annotation { "Feature Type Name" : "Feature", "Feature Type Description" : "" }
export const myFeature = defineFeature(function(context is Context, id is Id, definition is map)
    precondition{}
    {
        {
            var Q0;
            Q0=qCreatedBy(makeId("Top.planeOp"),FACE);
            var sketch = newSketch(context, id + "F0", { "sketchPlane" : qUnion([Q0])});
            skLineSegment(sketch, "E0.bottom", {"start": v(0, 0) * mm, "end": v(112.25, 0) * mm});
            skLineSegment(sketch, "E0.top", {"start": v(0, 107.75) * mm, "end": v(112.25, 107.75) * mm});
            skLineSegment(sketch, "E0.left", {"start": v(0, 0) * mm, "end": v(0, 107.75) * mm});
            skLineSegment(sketch, "E0.right", {"start": v(112.25, 0) * mm, "end": v(112.25, 107.75) * mm});
            skCircle(sketch, "E1", {"center": v(3.5, 3.5) * mm, "radius": 2.25 * mm});
            skCircle(sketch, "E2", {"center": v(108.75, 3.5) * mm, "radius": 2.25 * mm});
            skCircle(sketch, "E3", {"center": v(92.23, 18.3) * mm, "radius": 10.5 * mm});
            skCircle(sketch, "E4", {"center": v(60, 18.3) * mm, "radius": 3 * mm});
            skLineSegment(sketch, "E5.bottom", {"start": v(68.73, 26.3) * mm, "end": v(78.73, 26.3) * mm});
            skLineSegment(sketch, "E5.top", {"start": v(68.73, 24.3) * mm, "end": v(78.73, 24.3) * mm});
            skLineSegment(sketch, "E5.left", {"start": v(68.73, 26.3) * mm, "end": v(68.73, 24.3) * mm});
            skLineSegment(sketch, "E5.right", {"start": v(78.73, 26.3) * mm, "end": v(78.73, 24.3) * mm});
            skLineSegment(sketch, "E6.1.0.0", {"start": v(78.8, 22.4) * mm, "end": v(78.8, 20.4) * mm});
            skLineSegment(sketch, "E6.1.0.1", {"start": v(68.8, 22.4) * mm, "end": v(68.8, 20.4) * mm});
            skLineSegment(sketch, "E6.1.0.2", {"start": v(68.8, 22.4) * mm, "end": v(78.8, 22.4) * mm});
            skLineSegment(sketch, "E6.1.0.3", {"start": v(68.8, 20.4) * mm, "end": v(78.8, 20.4) * mm});
            skLineSegment(sketch, "E6.2.0.0", {"start": v(78.87, 18.5) * mm, "end": v(78.87, 16.5) * mm});
            skLineSegment(sketch, "E6.2.0.1", {"start": v(68.87, 18.5) * mm, "end": v(68.87, 16.5) * mm});
            skLineSegment(sketch, "E6.2.0.2", {"start": v(68.87, 18.5) * mm, "end": v(78.87, 18.5) * mm});
            skLineSegment(sketch, "E6.2.0.3", {"start": v(68.87, 16.5) * mm, "end": v(78.87, 16.5) * mm});
            skLineSegment(sketch, "E6.3.0.0", {"start": v(78.93, 14.62) * mm, "end": v(78.93, 12.62) * mm});
            skLineSegment(sketch, "E6.3.0.1", {"start": v(68.93, 14.62) * mm, "end": v(68.93, 12.62) * mm});
            skLineSegment(sketch, "E6.3.0.2", {"start": v(68.93, 14.62) * mm, "end": v(78.93, 14.62) * mm});
            skLineSegment(sketch, "E6.3.0.3", {"start": v(68.93, 12.62) * mm, "end": v(78.93, 12.62) * mm});
            skLineSegment(sketch, "E6.4.0.0", {"start": v(79, 10.73) * mm, "end": v(79, 8.73) * mm});
            skLineSegment(sketch, "E6.4.0.1", {"start": v(69, 10.73) * mm, "end": v(69, 8.73) * mm});
            skLineSegment(sketch, "E6.4.0.2", {"start": v(69, 10.73) * mm, "end": v(79, 10.73) * mm});
            skLineSegment(sketch, "E6.4.0.3", {"start": v(69, 8.73) * mm, "end": v(79, 8.73) * mm});
            skLineSegment(sketch, "E6.direction1", {"start": v(68.73, 24.3) * mm, "end": v(68.8, 20.4) * mm, "construction": true});
            skSolve(sketch);
        }
        {
            var Q0;
            Q0=qSketchRegion(id+"F0",true);
            extrude(context, id + "F1", {"entities" : qUnion([Q0]), "depth" : 2 * mm, "offsetDistance" : 25 * mm});
        }
        {
            var Q0;
            Q0=makeQuery(id+"F1.opExtrude","CAP_FACE",FACE,{"disambiguationData":[OSD([sQuery(id+"F0.wireOp",EDGE,"E0.bottom"),sQuery(id+"F0.wireOp",EDGE,"E0.top"),sQuery(id+"F0.wireOp",EDGE,"E0.left"),sQuery(id+"F0.wireOp",EDGE,"E0.right"),sQuery(id+"F0.wireOp",EDGE,"VJWhoFmN-CNNd-a6gC-JCuR-XAWFigalHExP"),sQuery(id+"F0.wireOp",EDGE,"vIjKD9R8-VXcQ-Syzh-FnhK-4sEpH6Cil4JO"),sQuery(id+"F0.wireOp",EDGE,"E1"),sQuery(id+"F0.wireOp",EDGE,"E2"),sQuery(id+"F0.wireOp",EDGE,"RQaqiYP4-0Fcv-lfBv-gB3g-qDtZXz7Vt3Ng.bottom"),sQuery(id+"F0.wireOp",EDGE,"RQaqiYP4-0Fcv-lfBv-gB3g-qDtZXz7Vt3Ng.top"),sQuery(id+"F0.wireOp",EDGE,"RQaqiYP4-0Fcv-lfBv-gB3g-qDtZXz7Vt3Ng.left"),sQuery(id+"F0.wireOp",EDGE,"RQaqiYP4-0Fcv-lfBv-gB3g-qDtZXz7Vt3Ng.right"),sQuery(id+"F0.wireOp",EDGE,"E3"),sQuery(id+"F0.wireOp",EDGE,"E4"),sQuery(id+"F0.wireOp",EDGE,"A4T1cfBq-erl5-skMh-XZ60-SgpOEBQzwWt8"),sQuery(id+"F0.wireOp",EDGE,"E5.bottom"),sQuery(id+"F0.wireOp",EDGE,"E5.top"),sQuery(id+"F0.wireOp",EDGE,"E5.left"),sQuery(id+"F0.wireOp",EDGE,"E5.right"),sQuery(id+"F0.wireOp",EDGE,"E6.1.0.0"),sQuery(id+"F0.wireOp",EDGE,"E6.1.0.1"),sQuery(id+"F0.wireOp",EDGE,"E6.1.0.2"),sQuery(id+"F0.wireOp",EDGE,"E6.1.0.3"),sQuery(id+"F0.wireOp",EDGE,"E6.2.0.0"),sQuery(id+"F0.wireOp",EDGE,"E6.2.0.1"),sQuery(id+"F0.wireOp",EDGE,"E6.2.0.2"),sQuery(id+"F0.wireOp",EDGE,"E6.2.0.3"),sQuery(id+"F0.wireOp",EDGE,"E6.3.0.0"),sQuery(id+"F0.wireOp",EDGE,"E6.3.0.1"),sQuery(id+"F0.wireOp",EDGE,"E6.3.0.2"),sQuery(id+"F0.wireOp",EDGE,"E6.3.0.3"),sQuery(id+"F0.wireOp",EDGE,"E6.4.0.0"),sQuery(id+"F0.wireOp",EDGE,"E6.4.0.1"),sQuery(id+"F0.wireOp",EDGE,"E6.4.0.2"),sQuery(id+"F0.wireOp",EDGE,"E6.4.0.3")])],"isStart":false});
            var sketch = newSketch(context, id + "F2", { "sketchPlane" : qUnion([Q0])});
            skLineSegment(sketch, "E7.bottom", {"start": v(49.13, 110.75) * mm, "end": v(61.13, 110.75) * mm});
            skLineSegment(sketch, "E7.top", {"start": v(49.13, 104.75) * mm, "end": v(61.13, 104.75) * mm});
            skLineSegment(sketch, "E7.left", {"start": v(49.13, 110.75) * mm, "end": v(49.13, 104.75) * mm});
            skLineSegment(sketch, "E7.right", {"start": v(61.13, 110.75) * mm, "end": v(61.13, 104.75) * mm});
            skSolve(sketch);
        }
        {
            var Q0;
            Q0=qSketchRegion(id+"F2",true);
            extrude(context, id + "F3", {"entities" : qUnion([Q0]), "operationType" : NewBodyOperationType.REMOVE, "endBound" : BoundingType.THROUGH_ALL, "oppositeDirection" : true, "depth" : 3 * mm, "offsetDistance" : 25 * mm});
        }
        {
            var Q0;
            {var subQ27=sQuery(id+"F0.wireOp",EDGE,"E0.left");var subQ29=sQuery(id+"F0.wireOp",EDGE,"E0.bottom");Q0=makeQuery(id+"F3.boolean.opBoolean","SPLIT",FACE,{"disambiguationData":[TD([makeQuery(id+"F1.opExtrude","SWEPT_FACE",FACE,{"disambiguationData":[OSD([subQ27])]})])],"derivedFrom":makeQuery(id+"F1.opExtrude","SWEPT_FACE",FACE,{"disambiguationData":[OSD([subQ29])]})});}
            var Q1;
            {var subQ26=sQuery(id+"F0.wireOp",EDGE,"E0.right");var subQ29=sQuery(id+"F0.wireOp",EDGE,"E0.bottom");Q1=makeQuery(id+"F3.boolean.opBoolean","SPLIT",FACE,{"disambiguationData":[TD([makeQuery(id+"F1.opExtrude","SWEPT_FACE",FACE,{"disambiguationData":[OSD([subQ26])]})])],"derivedFrom":makeQuery(id+"F1.opExtrude","SWEPT_FACE",FACE,{"disambiguationData":[OSD([subQ29])]})});}
            extrude(context, id + "F4", {"entities" : qUnion([Q0, Q1]), "operationType" : NewBodyOperationType.ADD, "depth" : 6 * mm, "offsetDistance" : 25 * mm});
        }
        {
            var Q0;
            {var subQ27=sQuery(id+"F0.wireOp",EDGE,"E0.left");var subQ28=sQuery(id+"F0.wireOp",EDGE,"E0.top");Q0=makeQuery(id+"F3.boolean.opBoolean","SPLIT",FACE,{"disambiguationData":[TD([makeQuery(id+"F1.opExtrude","SWEPT_FACE",FACE,{"disambiguationData":[OSD([subQ28])]})])],"derivedFrom":makeQuery(id+"F1.opExtrude","SWEPT_FACE",FACE,{"disambiguationData":[OSD([subQ27])]})});}
            var Q1;
            {var subQ0=sQuery(id+"F0.wireOp",EDGE,"E0.left");var subQ1=sQuery(id+"F0.wireOp",EDGE,"E0.bottom");Q1=makeQuery(id+"F4.boolean.opBoolean","MERGE",FACE,{"derivedFrom":[makeQuery(id+"F3.boolean.opBoolean","SPLIT",FACE,{"disambiguationData":[TD([makeQuery(id+"F1.opExtrude","SWEPT_FACE",FACE,{"disambiguationData":[OSD([subQ1])]})])],"derivedFrom":makeQuery(id+"F1.opExtrude","SWEPT_FACE",FACE,{"disambiguationData":[OSD([subQ0])]})}),makeQuery(id+"F4.opExtrude","SWEPT_FACE",FACE,{"disambiguationData":[OSD([subQ1,subQ0])]})]});}
            extrude(context, id + "F5", {"entities" : qUnion([Q0, Q1]), "operationType" : NewBodyOperationType.ADD, "depth" : 6 * mm, "offsetDistance" : 25 * mm});
        }
        {
            var Q0;
            {var subQ26=sQuery(id+"F0.wireOp",EDGE,"E0.right");var subQ28=sQuery(id+"F0.wireOp",EDGE,"E0.top");Q0=makeQuery(id+"F3.boolean.opBoolean","SPLIT",FACE,{"disambiguationData":[TD([makeQuery(id+"F1.opExtrude","SWEPT_FACE",FACE,{"disambiguationData":[OSD([subQ28])]})])],"derivedFrom":makeQuery(id+"F1.opExtrude","SWEPT_FACE",FACE,{"disambiguationData":[OSD([subQ26])]})});}
            var Q1;
            {var subQ0=sQuery(id+"F0.wireOp",EDGE,"E0.right");var subQ1=sQuery(id+"F0.wireOp",EDGE,"E0.bottom");Q1=makeQuery(id+"F4.boolean.opBoolean","MERGE",FACE,{"derivedFrom":[makeQuery(id+"F3.boolean.opBoolean","SPLIT",FACE,{"disambiguationData":[TD([makeQuery(id+"F1.opExtrude","SWEPT_FACE",FACE,{"disambiguationData":[OSD([subQ1])]})])],"derivedFrom":makeQuery(id+"F1.opExtrude","SWEPT_FACE",FACE,{"disambiguationData":[OSD([subQ0])]})}),makeQuery(id+"F4.opExtrude","SWEPT_FACE",FACE,{"disambiguationData":[OSD([subQ1,subQ0])]})]});}
            extrude(context, id + "F6", {"entities" : qUnion([Q0, Q1]), "operationType" : NewBodyOperationType.ADD, "depth" : 6 * mm, "offsetDistance" : 25 * mm});
        }
        {
            var Q0;
            {var subQ0=sQuery(id+"F0.wireOp",EDGE,"E0.right");var subQ1=sQuery(id+"F0.wireOp",EDGE,"E0.bottom");var subQ2=makeQuery(id+"F1.opExtrude","SWEPT_FACE",FACE,{"disambiguationData":[OSD([subQ1])]});var subQ3=makeQuery(id+"F1.opExtrude","SWEPT_FACE",FACE,{"disambiguationData":[OSD([subQ0])]});var subQ4=sQuery(id+"F0.wireOp",EDGE,"E0.left");var subQ5=sQuery(id+"F0.wireOp",EDGE,"E0.top");var subQ6=makeQuery(id+"F1.opExtrude","CAP_FACE",FACE,{"disambiguationData":[OSD([subQ1,subQ5,subQ4,subQ0,sQuery(id+"F0.wireOp",EDGE,"VJWhoFmN-CNNd-a6gC-JCuR-XAWFigalHExP"),sQuery(id+"F0.wireOp",EDGE,"vIjKD9R8-VXcQ-Syzh-FnhK-4sEpH6Cil4JO"),sQuery(id+"F0.wireOp",EDGE,"E1"),sQuery(id+"F0.wireOp",EDGE,"E2"),sQuery(id+"F0.wireOp",EDGE,"E3"),sQuery(id+"F0.wireOp",EDGE,"E4"),sQuery(id+"F0.wireOp",EDGE,"E5.bottom"),sQuery(id+"F0.wireOp",EDGE,"E5.top"),sQuery(id+"F0.wireOp",EDGE,"E5.left"),sQuery(id+"F0.wireOp",EDGE,"E5.right"),sQuery(id+"F0.wireOp",EDGE,"E6.1.0.0"),sQuery(id+"F0.wireOp",EDGE,"E6.1.0.1"),sQuery(id+"F0.wireOp",EDGE,"E6.1.0.2"),sQuery(id+"F0.wireOp",EDGE,"E6.1.0.3"),sQuery(id+"F0.wireOp",EDGE,"E6.2.0.0"),sQuery(id+"F0.wireOp",EDGE,"E6.2.0.1"),sQuery(id+"F0.wireOp",EDGE,"E6.2.0.2"),sQuery(id+"F0.wireOp",EDGE,"E6.2.0.3"),sQuery(id+"F0.wireOp",EDGE,"E6.3.0.0"),sQuery(id+"F0.wireOp",EDGE,"E6.3.0.1"),sQuery(id+"F0.wireOp",EDGE,"E6.3.0.2"),sQuery(id+"F0.wireOp",EDGE,"E6.3.0.3"),sQuery(id+"F0.wireOp",EDGE,"E6.4.0.0"),sQuery(id+"F0.wireOp",EDGE,"E6.4.0.1"),sQuery(id+"F0.wireOp",EDGE,"E6.4.0.2"),sQuery(id+"F0.wireOp",EDGE,"E6.4.0.3")])],"isStart":true});var subQ7=makeQuery(id+"F1.opExtrude","CAP_EDGE",EDGE,{"disambiguationData":[OSD([subQ0])],"isStart":true});var subQ8=makeQuery(id+"F1.opExtrude","SWEPT_FACE",FACE,{"disambiguationData":[OSD([subQ5])]});var subQ9=makeQuery(id+"F1.opExtrude","SWEPT_FACE",FACE,{"disambiguationData":[OSD([subQ4])]});var subQ10=makeQuery(id+"F1.opExtrude","CAP_EDGE",EDGE,{"disambiguationData":[OSD([subQ4])],"isStart":true});var subQ11=makeQuery(id+"F1.opExtrude","CAP_EDGE",EDGE,{"disambiguationData":[OSD([subQ1])],"isStart":true});Q0=makeQuery(id+"F6.boolean.opBoolean","MERGE",FACE,{"derivedFrom":[makeQuery(id+"F5.boolean.opBoolean","MERGE",FACE,{"derivedFrom":[makeQuery(id+"F4.boolean.opBoolean","MERGE",FACE,{"derivedFrom":[subQ6,makeQuery(id+"F4.opExtrude","SWEPT_FACE",FACE,{"disambiguationData":[OSD([subQ1]),TDD([makeQuery(id+"F3.boolean.opBoolean","SPLIT",EDGE,{"disambiguationData":[TD([subQ9])],"derivedFrom":subQ11})])]}),makeQuery(id+"F4.opExtrude","SWEPT_FACE",FACE,{"disambiguationData":[OSD([subQ1]),TDD([makeQuery(id+"F3.boolean.opBoolean","SPLIT",EDGE,{"disambiguationData":[TD([subQ3])],"derivedFrom":subQ11})])]})]}),makeQuery(id+"F5.opExtrude","SWEPT_FACE",FACE,{"disambiguationData":[OSD([subQ4]),TDD([makeQuery(id+"F3.boolean.opBoolean","SPLIT",EDGE,{"disambiguationData":[TD([subQ8])],"derivedFrom":subQ10})])]}),makeQuery(id+"F5.opExtrude","SWEPT_FACE",FACE,{"disambiguationData":[OSD([subQ1,subQ4]),TDD([makeQuery(id+"F4.boolean.opBoolean","MERGE",EDGE,{"derivedFrom":[makeQuery(id+"F3.boolean.opBoolean","SPLIT",EDGE,{"disambiguationData":[TD([subQ2])],"derivedFrom":subQ10}),makeQuery(id+"F4.opExtrude","SWEPT_EDGE",EDGE,{"disambiguationData":[OSD([subQ1,subQ4]),TDD([makeQuery(id+"F1.opExtrude","CAP_VERTEX",VERTEX,{"disambiguationData":[OSD([subQ1,subQ4])],"isStart":true})])]})]})])]})]}),makeQuery(id+"F6.opExtrude","SWEPT_FACE",FACE,{"disambiguationData":[OSD([subQ0]),TDD([makeQuery(id+"F3.boolean.opBoolean","SPLIT",EDGE,{"disambiguationData":[TD([subQ8])],"derivedFrom":subQ7})])]}),makeQuery(id+"F6.opExtrude","SWEPT_FACE",FACE,{"disambiguationData":[OSD([subQ1,subQ0]),TDD([makeQuery(id+"F4.boolean.opBoolean","MERGE",EDGE,{"derivedFrom":[makeQuery(id+"F3.boolean.opBoolean","SPLIT",EDGE,{"disambiguationData":[TD([subQ2])],"derivedFrom":subQ7}),makeQuery(id+"F4.opExtrude","SWEPT_EDGE",EDGE,{"disambiguationData":[OSD([subQ1,subQ0]),TDD([makeQuery(id+"F1.opExtrude","CAP_VERTEX",VERTEX,{"disambiguationData":[OSD([subQ1,subQ0])],"isStart":true})])]})]})])]})]});}
            var sketch = newSketch(context, id + "F7", { "sketchPlane" : qUnion([Q0])});
            skLineSegment(sketch, "E8.bottom", {"start": v(118.25, -107.75) * mm, "end": v(116.75, -107.75) * mm});
            skLineSegment(sketch, "E8.top", {"start": v(118.25, 6) * mm, "end": v(116.75, 6) * mm});
            skLineSegment(sketch, "E8.left", {"start": v(118.25, -107.75) * mm, "end": v(118.25, -107.75) * mm});
            skLineSegment(sketch, "E8.right", {"start": v(116.75, -107.75) * mm, "end": v(116.75, -58.87) * mm});
            skLineSegment(sketch, "E9.bottom", {"start": v(-6, -107.75) * mm, "end": v(-4.5, -107.75) * mm});
            skLineSegment(sketch, "E9.top", {"start": v(-6, 6) * mm, "end": v(-4.5, 6) * mm});
            skLineSegment(sketch, "E9.left", {"start": v(-6, -107.75) * mm, "end": v(-6, -107.75) * mm});
            skLineSegment(sketch, "E9.right", {"start": v(-4.5, -107.75) * mm, "end": v(-4.5, -58.87) * mm});
            skLineSegment(sketch, "E10.bottom", {"start": v(116.75, 4.5) * mm, "end": v(61.13, 4.5) * mm});
            skLineSegment(sketch, "E10.top", {"start": v(116.75, 6) * mm, "end": v(61.13, 6) * mm});
            skLineSegment(sketch, "E11.trimOffspring", {"start": v(61.13, 4.5) * mm, "end": v(-4.5, 4.5) * mm});
            skLineSegment(sketch, "E12.trimOffspring", {"start": v(61.13, 6) * mm, "end": v(-4.5, 6) * mm});
            skLineSegment(sketch, "E13.trimOffspring", {"start": v(118.25, -107.75) * mm, "end": v(118.25, 6) * mm});
            skLineSegment(sketch, "E14.trimOffspring", {"start": v(116.75, -58.87) * mm, "end": v(116.75, 4.5) * mm});
            skLineSegment(sketch, "E15.trimOffspring", {"start": v(-4.5, -58.87) * mm, "end": v(-4.5, 4.5) * mm});
            skLineSegment(sketch, "E16.trimOffspring", {"start": v(-6, -107.75) * mm, "end": v(-6, 6) * mm});
            skSolve(sketch);
        }
        {
            var Q0;
            {var subQ43=sQuery(id+"F7.wireOp",EDGE,"E9.top");Q0=makeQuery(id+"F7.imprint","IMPRINT",FACE,{"disambiguationData":[TD([[makeQuery(id+"F7.imprint","IMPRINT",EDGE,{"derivedFrom":subQ43}),-1.0]])]});}
            var Q1;
            {var subQ0=sQuery(id+"F7.wireOp",EDGE,"E11.trimOffspring");var subQ2=sQuery(id+"F0.wireOp",EDGE,"E6.4.0.3");var subQ3=sQuery(id+"F0.wireOp",EDGE,"E6.4.0.2");var subQ4=sQuery(id+"F0.wireOp",EDGE,"E6.4.0.1");var subQ5=sQuery(id+"F0.wireOp",EDGE,"E6.4.0.0");var subQ6=sQuery(id+"F0.wireOp",EDGE,"E6.3.0.3");var subQ7=sQuery(id+"F0.wireOp",EDGE,"E6.3.0.2");var subQ8=sQuery(id+"F0.wireOp",EDGE,"E6.3.0.1");var subQ9=sQuery(id+"F0.wireOp",EDGE,"E6.3.0.0");var subQ10=sQuery(id+"F0.wireOp",EDGE,"E6.2.0.3");var subQ11=sQuery(id+"F0.wireOp",EDGE,"E6.2.0.2");var subQ12=sQuery(id+"F0.wireOp",EDGE,"E6.2.0.1");var subQ13=sQuery(id+"F0.wireOp",EDGE,"E6.2.0.0");var subQ14=sQuery(id+"F0.wireOp",EDGE,"E6.1.0.3");var subQ15=sQuery(id+"F0.wireOp",EDGE,"E6.1.0.2");var subQ16=sQuery(id+"F0.wireOp",EDGE,"E6.1.0.1");var subQ17=sQuery(id+"F0.wireOp",EDGE,"E6.1.0.0");var subQ18=sQuery(id+"F0.wireOp",EDGE,"E5.right");var subQ19=sQuery(id+"F0.wireOp",EDGE,"E5.left");var subQ20=sQuery(id+"F0.wireOp",EDGE,"E5.top");var subQ21=sQuery(id+"F0.wireOp",EDGE,"E5.bottom");var subQ22=sQuery(id+"F0.wireOp",EDGE,"E4");var subQ23=sQuery(id+"F0.wireOp",EDGE,"E3");var subQ24=sQuery(id+"F0.wireOp",EDGE,"E2");var subQ25=sQuery(id+"F0.wireOp",EDGE,"E1");var subQ26=sQuery(id+"F0.wireOp",EDGE,"vIjKD9R8-VXcQ-Syzh-FnhK-4sEpH6Cil4JO");var subQ27=sQuery(id+"F0.wireOp",EDGE,"VJWhoFmN-CNNd-a6gC-JCuR-XAWFigalHExP");var subQ28=sQuery(id+"F0.wireOp",EDGE,"E0.right");var subQ29=sQuery(id+"F0.wireOp",EDGE,"E0.left");var subQ30=sQuery(id+"F0.wireOp",EDGE,"E0.top");var subQ31=sQuery(id+"F0.wireOp",EDGE,"E0.bottom");var subQ32=makeQuery(id+"F1.opExtrude","CAP_FACE",FACE,{"disambiguationData":[OSD([subQ31,subQ30,subQ29,subQ28,subQ27,subQ26,subQ25,subQ24,subQ23,subQ22,subQ21,subQ20,subQ19,subQ18,subQ17,subQ16,subQ15,subQ14,subQ13,subQ12,subQ11,subQ10,subQ9,subQ8,subQ7,subQ6,subQ5,subQ4,subQ3,subQ2])],"isStart":true});var subQ35=sQuery(id+"F2.wireOp",EDGE,"RaCBA7yH-dog8-7tBN-7lt1-G5SoJbxULKHr.left");var subQ36=makeQuery(id+"F4.boolean.opBoolean","MERGE",EDGE,{"derivedFrom":[makeQuery(id+"F3.boolean.opBoolean","INTERSECT",EDGE,{"derivedFrom":[subQ32,makeQuery(id+"F3.opExtrude","SWEPT_FACE",FACE,{"disambiguationData":[OSD([subQ35])]})]}),makeQuery(id+"F4.opExtrude","SWEPT_EDGE",EDGE,{"disambiguationData":[OSD([subQ31,subQ30,subQ29,subQ28,subQ27,subQ26,subQ25,subQ24,subQ23,subQ22,subQ21,subQ20,subQ19,subQ18,subQ17,subQ16,subQ15,subQ14,subQ13,subQ12,subQ11,subQ10,subQ9,subQ8,subQ7,subQ6,subQ5,subQ4,subQ3,subQ2,subQ35])]})]});var subQ37=makeQuery(id+"F7.imprint","INTERSECT",VERTEX,{"derivedFrom":[subQ36,subQ0]});Q1=makeQuery(id+"F7.imprint","IMPRINT",FACE,{"disambiguationData":[TD([[makeQuery(id+"F7.imprint","IMPRINT",EDGE,{"disambiguationData":[TD([[subQ37,1.0]])],"derivedFrom":subQ0}),-1.0]])]});}
            var Q2;
            {var subQ35=sQuery(id+"F7.wireOp",EDGE,"E8.top");Q2=makeQuery(id+"F7.imprint","IMPRINT",FACE,{"disambiguationData":[TD([[makeQuery(id+"F7.imprint","IMPRINT",EDGE,{"derivedFrom":subQ35}),-1.0]])]});}
            var Q3;
            {var subQ0=sQuery(id+"F7.wireOp",EDGE,"E15.trimOffspring");var subQ2=sQuery(id+"F0.wireOp",EDGE,"E6.4.0.3");var subQ3=sQuery(id+"F0.wireOp",EDGE,"E6.4.0.2");var subQ4=sQuery(id+"F0.wireOp",EDGE,"E6.4.0.1");var subQ5=sQuery(id+"F0.wireOp",EDGE,"E6.4.0.0");var subQ6=sQuery(id+"F0.wireOp",EDGE,"E6.3.0.3");var subQ7=sQuery(id+"F0.wireOp",EDGE,"E6.3.0.2");var subQ8=sQuery(id+"F0.wireOp",EDGE,"E6.3.0.1");var subQ9=sQuery(id+"F0.wireOp",EDGE,"E6.3.0.0");var subQ10=sQuery(id+"F0.wireOp",EDGE,"E6.2.0.3");var subQ11=sQuery(id+"F0.wireOp",EDGE,"E6.2.0.2");var subQ12=sQuery(id+"F0.wireOp",EDGE,"E6.2.0.1");var subQ13=sQuery(id+"F0.wireOp",EDGE,"E6.2.0.0");var subQ14=sQuery(id+"F0.wireOp",EDGE,"E6.1.0.3");var subQ15=sQuery(id+"F0.wireOp",EDGE,"E6.1.0.2");var subQ16=sQuery(id+"F0.wireOp",EDGE,"E6.1.0.1");var subQ17=sQuery(id+"F0.wireOp",EDGE,"E6.1.0.0");var subQ18=sQuery(id+"F0.wireOp",EDGE,"E5.right");var subQ19=sQuery(id+"F0.wireOp",EDGE,"E5.left");var subQ20=sQuery(id+"F0.wireOp",EDGE,"E5.top");var subQ21=sQuery(id+"F0.wireOp",EDGE,"E5.bottom");var subQ22=sQuery(id+"F0.wireOp",EDGE,"E4");var subQ23=sQuery(id+"F0.wireOp",EDGE,"E3");var subQ24=sQuery(id+"F0.wireOp",EDGE,"E2");var subQ25=sQuery(id+"F0.wireOp",EDGE,"E1");var subQ26=sQuery(id+"F0.wireOp",EDGE,"vIjKD9R8-VXcQ-Syzh-FnhK-4sEpH6Cil4JO");var subQ27=sQuery(id+"F0.wireOp",EDGE,"VJWhoFmN-CNNd-a6gC-JCuR-XAWFigalHExP");var subQ28=sQuery(id+"F0.wireOp",EDGE,"E0.right");var subQ29=sQuery(id+"F0.wireOp",EDGE,"E0.left");var subQ30=sQuery(id+"F0.wireOp",EDGE,"E0.top");var subQ31=sQuery(id+"F0.wireOp",EDGE,"E0.bottom");var subQ32=makeQuery(id+"F1.opExtrude","CAP_FACE",FACE,{"disambiguationData":[OSD([subQ31,subQ30,subQ29,subQ28,subQ27,subQ26,subQ25,subQ24,subQ23,subQ22,subQ21,subQ20,subQ19,subQ18,subQ17,subQ16,subQ15,subQ14,subQ13,subQ12,subQ11,subQ10,subQ9,subQ8,subQ7,subQ6,subQ5,subQ4,subQ3,subQ2])],"isStart":true});var subQ35=sQuery(id+"F2.wireOp",EDGE,"B4hFqdSQ-0Typ-vqDE-Ih2C-VjGMQgmkNHEO.top");var subQ36=makeQuery(id+"F5.boolean.opBoolean","MERGE",EDGE,{"derivedFrom":[makeQuery(id+"F3.boolean.opBoolean","INTERSECT",EDGE,{"derivedFrom":[subQ32,makeQuery(id+"F3.opExtrude","SWEPT_FACE",FACE,{"disambiguationData":[OSD([subQ35])]})]}),makeQuery(id+"F5.opExtrude","SWEPT_EDGE",EDGE,{"disambiguationData":[OSD([subQ31,subQ30,subQ29,subQ28,subQ27,subQ26,subQ25,subQ24,subQ23,subQ22,subQ21,subQ20,subQ19,subQ18,subQ17,subQ16,subQ15,subQ14,subQ13,subQ12,subQ11,subQ10,subQ9,subQ8,subQ7,subQ6,subQ5,subQ4,subQ3,subQ2,subQ35])]})]});var subQ37=makeQuery(id+"F7.imprint","INTERSECT",VERTEX,{"derivedFrom":[subQ36,subQ0]});Q3=makeQuery(id+"F7.imprint","IMPRINT",FACE,{"disambiguationData":[TD([[makeQuery(id+"F7.imprint","IMPRINT",EDGE,{"disambiguationData":[TD([[subQ37,1.0]])],"derivedFrom":subQ0}),1.0]])]});}
            var Q4;
            Q4=makeQuery(id+"F7.imprint","IMPRINT",FACE,{"disambiguationData":[TD([[makeQuery(id+"F7.imprint","IMPRINT",EDGE,{"derivedFrom":sQuery(id+"F7.wireOp",EDGE,"E9.bottom")}),1.0]])]});
            var Q5;
            {var subQ0=sQuery(id+"F7.wireOp",EDGE,"E13.trimOffspring");var subQ1=sQuery(id+"F2.wireOp",EDGE,"Su4fTRgq-EHtu-sVLe-Fh6S-CbHE7HdcJEhx.bottom");var subQ2=sQuery(id+"F0.wireOp",EDGE,"E6.4.0.3");var subQ3=sQuery(id+"F0.wireOp",EDGE,"E6.4.0.2");var subQ4=sQuery(id+"F0.wireOp",EDGE,"E6.4.0.1");var subQ5=sQuery(id+"F0.wireOp",EDGE,"E6.4.0.0");var subQ6=sQuery(id+"F0.wireOp",EDGE,"E6.3.0.3");var subQ7=sQuery(id+"F0.wireOp",EDGE,"E6.3.0.2");var subQ8=sQuery(id+"F0.wireOp",EDGE,"E6.3.0.1");var subQ9=sQuery(id+"F0.wireOp",EDGE,"E6.3.0.0");var subQ10=sQuery(id+"F0.wireOp",EDGE,"E6.2.0.3");var subQ11=sQuery(id+"F0.wireOp",EDGE,"E6.2.0.2");var subQ12=sQuery(id+"F0.wireOp",EDGE,"E6.2.0.1");var subQ13=sQuery(id+"F0.wireOp",EDGE,"E6.2.0.0");var subQ14=sQuery(id+"F0.wireOp",EDGE,"E6.1.0.3");var subQ15=sQuery(id+"F0.wireOp",EDGE,"E6.1.0.2");var subQ16=sQuery(id+"F0.wireOp",EDGE,"E6.1.0.1");var subQ17=sQuery(id+"F0.wireOp",EDGE,"E6.1.0.0");var subQ18=sQuery(id+"F0.wireOp",EDGE,"E5.right");var subQ19=sQuery(id+"F0.wireOp",EDGE,"E5.left");var subQ20=sQuery(id+"F0.wireOp",EDGE,"E5.top");var subQ21=sQuery(id+"F0.wireOp",EDGE,"E5.bottom");var subQ22=sQuery(id+"F0.wireOp",EDGE,"E4");var subQ23=sQuery(id+"F0.wireOp",EDGE,"E3");var subQ24=sQuery(id+"F0.wireOp",EDGE,"E2");var subQ25=sQuery(id+"F0.wireOp",EDGE,"E1");var subQ26=sQuery(id+"F0.wireOp",EDGE,"vIjKD9R8-VXcQ-Syzh-FnhK-4sEpH6Cil4JO");var subQ27=sQuery(id+"F0.wireOp",EDGE,"VJWhoFmN-CNNd-a6gC-JCuR-XAWFigalHExP");var subQ28=sQuery(id+"F0.wireOp",EDGE,"E0.right");var subQ29=sQuery(id+"F0.wireOp",EDGE,"E0.left");var subQ30=sQuery(id+"F0.wireOp",EDGE,"E0.top");var subQ31=sQuery(id+"F0.wireOp",EDGE,"E0.bottom");var subQ32=makeQuery(id+"F1.opExtrude","CAP_FACE",FACE,{"disambiguationData":[OSD([subQ31,subQ30,subQ29,subQ28,subQ27,subQ26,subQ25,subQ24,subQ23,subQ22,subQ21,subQ20,subQ19,subQ18,subQ17,subQ16,subQ15,subQ14,subQ13,subQ12,subQ11,subQ10,subQ9,subQ8,subQ7,subQ6,subQ5,subQ4,subQ3,subQ2])],"isStart":true});var subQ33=makeQuery(id+"F6.boolean.opBoolean","MERGE",EDGE,{"derivedFrom":[makeQuery(id+"F3.boolean.opBoolean","INTERSECT",EDGE,{"derivedFrom":[subQ32,makeQuery(id+"F3.opExtrude","SWEPT_FACE",FACE,{"disambiguationData":[OSD([subQ1])]})]}),makeQuery(id+"F6.opExtrude","SWEPT_EDGE",EDGE,{"disambiguationData":[OSD([subQ31,subQ30,subQ29,subQ28,subQ27,subQ26,subQ25,subQ24,subQ23,subQ22,subQ21,subQ20,subQ19,subQ18,subQ17,subQ16,subQ15,subQ14,subQ13,subQ12,subQ11,subQ10,subQ9,subQ8,subQ7,subQ6,subQ5,subQ4,subQ3,subQ2,subQ1])]})]});var subQ34=makeQuery(id+"F7.imprint","INTERSECT",VERTEX,{"derivedFrom":[subQ33,sQuery(id+"F7.wireOp",EDGE,"E8.left"),subQ0]});Q5=makeQuery(id+"F7.imprint","IMPRINT",FACE,{"disambiguationData":[TD([[makeQuery(id+"F7.imprint","IMPRINT",EDGE,{"disambiguationData":[TD([[subQ34,-1.0]])],"derivedFrom":subQ0}),1.0]])]});}
            var Q6;
            Q6=makeQuery(id+"F7.imprint","IMPRINT",FACE,{"disambiguationData":[TD([[makeQuery(id+"F7.imprint","IMPRINT",EDGE,{"derivedFrom":sQuery(id+"F7.wireOp",EDGE,"E8.bottom")}),1.0]])]});
            extrude(context, id + "F8", {"entities" : qUnion([Q0, Q1, Q2, Q3, Q4, Q5, Q6]), "operationType" : NewBodyOperationType.ADD, "depth" : 7 * mm, "offsetDistance" : 25 * mm});
        }
        {
            var Q0;
            {var subQ0=sQuery(id+"F0.wireOp",EDGE,"E0.right");var subQ1=sQuery(id+"F0.wireOp",EDGE,"E0.bottom");var subQ2=makeQuery(id+"F1.opExtrude","SWEPT_FACE",FACE,{"disambiguationData":[OSD([subQ1])]});var subQ3=makeQuery(id+"F1.opExtrude","SWEPT_FACE",FACE,{"disambiguationData":[OSD([subQ0])]});var subQ4=sQuery(id+"F0.wireOp",EDGE,"E0.left");var subQ5=sQuery(id+"F0.wireOp",EDGE,"E0.top");var subQ6=makeQuery(id+"F1.opExtrude","CAP_FACE",FACE,{"disambiguationData":[OSD([subQ1,subQ5,subQ4,subQ0,sQuery(id+"F0.wireOp",EDGE,"VJWhoFmN-CNNd-a6gC-JCuR-XAWFigalHExP"),sQuery(id+"F0.wireOp",EDGE,"vIjKD9R8-VXcQ-Syzh-FnhK-4sEpH6Cil4JO"),sQuery(id+"F0.wireOp",EDGE,"E1"),sQuery(id+"F0.wireOp",EDGE,"E2"),sQuery(id+"F0.wireOp",EDGE,"E3"),sQuery(id+"F0.wireOp",EDGE,"E4"),sQuery(id+"F0.wireOp",EDGE,"E5.bottom"),sQuery(id+"F0.wireOp",EDGE,"E5.top"),sQuery(id+"F0.wireOp",EDGE,"E5.left"),sQuery(id+"F0.wireOp",EDGE,"E5.right"),sQuery(id+"F0.wireOp",EDGE,"E6.1.0.0"),sQuery(id+"F0.wireOp",EDGE,"E6.1.0.1"),sQuery(id+"F0.wireOp",EDGE,"E6.1.0.2"),sQuery(id+"F0.wireOp",EDGE,"E6.1.0.3"),sQuery(id+"F0.wireOp",EDGE,"E6.2.0.0"),sQuery(id+"F0.wireOp",EDGE,"E6.2.0.1"),sQuery(id+"F0.wireOp",EDGE,"E6.2.0.2"),sQuery(id+"F0.wireOp",EDGE,"E6.2.0.3"),sQuery(id+"F0.wireOp",EDGE,"E6.3.0.0"),sQuery(id+"F0.wireOp",EDGE,"E6.3.0.1"),sQuery(id+"F0.wireOp",EDGE,"E6.3.0.2"),sQuery(id+"F0.wireOp",EDGE,"E6.3.0.3"),sQuery(id+"F0.wireOp",EDGE,"E6.4.0.0"),sQuery(id+"F0.wireOp",EDGE,"E6.4.0.1"),sQuery(id+"F0.wireOp",EDGE,"E6.4.0.2"),sQuery(id+"F0.wireOp",EDGE,"E6.4.0.3")])],"isStart":false});var subQ7=makeQuery(id+"F1.opExtrude","CAP_EDGE",EDGE,{"disambiguationData":[OSD([subQ0])],"isStart":false});var subQ8=makeQuery(id+"F1.opExtrude","SWEPT_FACE",FACE,{"disambiguationData":[OSD([subQ5])]});var subQ9=makeQuery(id+"F1.opExtrude","SWEPT_FACE",FACE,{"disambiguationData":[OSD([subQ4])]});var subQ10=makeQuery(id+"F1.opExtrude","CAP_EDGE",EDGE,{"disambiguationData":[OSD([subQ4])],"isStart":false});var subQ11=makeQuery(id+"F1.opExtrude","CAP_EDGE",EDGE,{"disambiguationData":[OSD([subQ1])],"isStart":false});Q0=makeQuery(id+"F6.boolean.opBoolean","MERGE",FACE,{"derivedFrom":[makeQuery(id+"F5.boolean.opBoolean","MERGE",FACE,{"derivedFrom":[makeQuery(id+"F4.boolean.opBoolean","MERGE",FACE,{"derivedFrom":[subQ6,makeQuery(id+"F4.opExtrude","SWEPT_FACE",FACE,{"disambiguationData":[OSD([subQ1]),TDD([makeQuery(id+"F3.boolean.opBoolean","SPLIT",EDGE,{"disambiguationData":[TD([subQ9])],"derivedFrom":subQ11})])]}),makeQuery(id+"F4.opExtrude","SWEPT_FACE",FACE,{"disambiguationData":[OSD([subQ1]),TDD([makeQuery(id+"F3.boolean.opBoolean","SPLIT",EDGE,{"disambiguationData":[TD([subQ3])],"derivedFrom":subQ11})])]})]}),makeQuery(id+"F5.opExtrude","SWEPT_FACE",FACE,{"disambiguationData":[OSD([subQ4]),TDD([makeQuery(id+"F3.boolean.opBoolean","SPLIT",EDGE,{"disambiguationData":[TD([subQ8])],"derivedFrom":subQ10})])]}),makeQuery(id+"F5.opExtrude","SWEPT_FACE",FACE,{"disambiguationData":[OSD([subQ1,subQ4]),TDD([makeQuery(id+"F4.boolean.opBoolean","MERGE",EDGE,{"derivedFrom":[makeQuery(id+"F3.boolean.opBoolean","SPLIT",EDGE,{"disambiguationData":[TD([subQ2])],"derivedFrom":subQ10}),makeQuery(id+"F4.opExtrude","SWEPT_EDGE",EDGE,{"disambiguationData":[OSD([subQ1,subQ4]),TDD([makeQuery(id+"F1.opExtrude","CAP_VERTEX",VERTEX,{"disambiguationData":[OSD([subQ1,subQ4])],"isStart":false})])]})]})])]})]}),makeQuery(id+"F6.opExtrude","SWEPT_FACE",FACE,{"disambiguationData":[OSD([subQ0]),TDD([makeQuery(id+"F3.boolean.opBoolean","SPLIT",EDGE,{"disambiguationData":[TD([subQ8])],"derivedFrom":subQ7})])]}),makeQuery(id+"F6.opExtrude","SWEPT_FACE",FACE,{"disambiguationData":[OSD([subQ1,subQ0]),TDD([makeQuery(id+"F4.boolean.opBoolean","MERGE",EDGE,{"derivedFrom":[makeQuery(id+"F3.boolean.opBoolean","SPLIT",EDGE,{"disambiguationData":[TD([subQ2])],"derivedFrom":subQ7}),makeQuery(id+"F4.opExtrude","SWEPT_EDGE",EDGE,{"disambiguationData":[OSD([subQ1,subQ0]),TDD([makeQuery(id+"F1.opExtrude","CAP_VERTEX",VERTEX,{"disambiguationData":[OSD([subQ1,subQ0])],"isStart":false})])]})]})])]})]});}
            var sketch = newSketch(context, id + "F9", { "sketchPlane" : qUnion([Q0])});
            skText(sketch, "E17", { "text": "Victor-CreatBot\n", "fontName": "OpenSans-Italic.ttf"});
            skText(sketch, "E18", { "text": "3D Printer", "fontName": "OpenSans-Italic.ttf"});
            skText(sketch, "E19", { "text": "and", "fontName": "OpenSans-Regular.ttf"});
            skText(sketch, "E20", { "text": "Laser Engraver", "fontName": "OpenSans-Italic.ttf"});
            skText(sketch, "E21", { "text": "Controller", "fontName": "OpenSans-Italic.ttf"});
            skText(sketch, "E22", { "text": "Proudly Singapore Crafted", "fontName": "OpenSans-Italic.ttf"});
            const initialGuessF9  = {"E17": [0.009, 0.08675, 1, 0, 0.01], "E18": [0.0307, 0.07375, 1, 0, 0.008], "E19": [0.044, 0.06075, 1, 0, 0.008], "E20": [0.019, 0.04775, 1, 0, 0.008], "E21": [0.0311, 0.03475, 1, 0, 0.008], "E22": [0, 0.0078, 1, 0, 0.004]};
            skSetInitialGuess(sketch, initialGuessF9);
            skSolve(sketch);
        }
        {
            var Q0;
            Q0=qSketchRegion(id+"F9",true);
            extrude(context, id + "F10", {"entities" : qUnion([Q0]), "operationType" : NewBodyOperationType.ADD, "depth" : 1.5 * mm, "offsetDistance" : 25 * mm});
        }
        {
            var Q0;
            {var subQ0=sQuery(id+"F0.wireOp",EDGE,"E0.left");var subQ1=sQuery(id+"F0.wireOp",EDGE,"E0.top");Q0=makeQuery(id+"F8.boolean.opBoolean","MERGE",FACE,{"derivedFrom":[makeQuery(id+"F5.boolean.opBoolean","MERGE",FACE,{"derivedFrom":[makeQuery(id+"F3.boolean.opBoolean","SPLIT",FACE,{"disambiguationData":[TD([makeQuery(id+"F1.opExtrude","SWEPT_FACE",FACE,{"disambiguationData":[OSD([subQ0])]})])],"derivedFrom":makeQuery(id+"F1.opExtrude","SWEPT_FACE",FACE,{"disambiguationData":[OSD([subQ1])]})}),makeQuery(id+"F5.opExtrude","SWEPT_FACE",FACE,{"disambiguationData":[OSD([subQ1,subQ0])]})]}),makeQuery(id+"F8.opExtrude","SWEPT_FACE",FACE,{"disambiguationData":[OSD([sQuery(id+"F7.wireOp",EDGE,"E9.bottom")])]})]});}
            var sketch = newSketch(context, id + "F11", { "sketchPlane" : qUnion([Q0])});
            skLineSegment(sketch, "E23.bottom", {"start": v(6, 2) * mm, "end": v(4.5, 2) * mm});
            skLineSegment(sketch, "E23.top", {"start": v(6, -7) * mm, "end": v(4.5, -7) * mm});
            skLineSegment(sketch, "E23.left", {"start": v(6, 2) * mm, "end": v(6, -7) * mm});
            skLineSegment(sketch, "E23.right", {"start": v(4.5, 2) * mm, "end": v(4.5, -7) * mm});
            skSolve(sketch);
        }
        {
            var Q0;
            {var subQ35=sQuery(id+"F11.wireOp",EDGE,"E23.bottom");Q0=makeQuery(id+"F11.imprint","IMPRINT",FACE,{"disambiguationData":[TD([[makeQuery(id+"F11.imprint","IMPRINT",EDGE,{"derivedFrom":subQ35}),1.0]])]});}
            extrude(context, id + "F12", {"entities" : qUnion([Q0]), "operationType" : NewBodyOperationType.ADD, "depth" : 10 * mm, "offsetDistance" : 25 * mm});
        }
        {
            var Q0;
            {var subQ0=sQuery(id+"F0.wireOp",EDGE,"E0.right");var subQ1=sQuery(id+"F0.wireOp",EDGE,"E0.top");Q0=makeQuery(id+"F8.boolean.opBoolean","MERGE",FACE,{"derivedFrom":[makeQuery(id+"F6.boolean.opBoolean","MERGE",FACE,{"derivedFrom":[makeQuery(id+"F3.boolean.opBoolean","SPLIT",FACE,{"disambiguationData":[TD([makeQuery(id+"F1.opExtrude","SWEPT_FACE",FACE,{"disambiguationData":[OSD([subQ0])]})])],"derivedFrom":makeQuery(id+"F1.opExtrude","SWEPT_FACE",FACE,{"disambiguationData":[OSD([subQ1])]})}),makeQuery(id+"F6.opExtrude","SWEPT_FACE",FACE,{"disambiguationData":[OSD([subQ1,subQ0])]})]}),makeQuery(id+"F8.opExtrude","SWEPT_FACE",FACE,{"disambiguationData":[OSD([sQuery(id+"F7.wireOp",EDGE,"E8.bottom")])]})]});}
            var sketch = newSketch(context, id + "F13", { "sketchPlane" : qUnion([Q0])});
            skLineSegment(sketch, "E24.bottom", {"start": v(-118.25, 2) * mm, "end": v(-116.75, 2) * mm});
            skLineSegment(sketch, "E24.top", {"start": v(-118.25, -7) * mm, "end": v(-116.75, -7) * mm});
            skLineSegment(sketch, "E24.left", {"start": v(-118.25, 2) * mm, "end": v(-118.25, -7) * mm});
            skLineSegment(sketch, "E24.right", {"start": v(-116.75, 2) * mm, "end": v(-116.75, -7) * mm});
            skSolve(sketch);
        }
        {
            var Q0;
            {var subQ35=sQuery(id+"F13.wireOp",EDGE,"E24.bottom");Q0=makeQuery(id+"F13.imprint","IMPRINT",FACE,{"disambiguationData":[TD([[makeQuery(id+"F13.imprint","IMPRINT",EDGE,{"derivedFrom":subQ35}),1.0]])]});}
            extrude(context, id + "F14", {"entities" : qUnion([Q0]), "operationType" : NewBodyOperationType.ADD, "depth" : 10 * mm, "offsetDistance" : 25 * mm});
        }
        {
            var Q0;
            Q0=makeQuery(id+"F8.opExtrude","SWEPT_FACE",FACE,{"disambiguationData":[OSD([sQuery(id+"F7.wireOp",EDGE,"E10.bottom"),sQuery(id+"F7.wireOp",EDGE,"E11.trimOffspring")])]});
            var sketch = newSketch(context, id + "F15", { "sketchPlane" : qUnion([Q0])});
            skLineSegment(sketch, "E25.bottom", {"start": v(-112.8, -7) * mm, "end": v(-92.8, -7) * mm});
            skLineSegment(sketch, "E25.top", {"start": v(-112.8, -5) * mm, "end": v(-92.8, -5) * mm});
            skLineSegment(sketch, "E25.left", {"start": v(-112.8, -7) * mm, "end": v(-112.8, -5) * mm});
            skLineSegment(sketch, "E25.right", {"start": v(-92.8, -7) * mm, "end": v(-92.8, -5) * mm});
            skLineSegment(sketch, "E26.bottom", {"start": v(0, -7) * mm, "end": v(-20, -7) * mm});
            skLineSegment(sketch, "E26.top", {"start": v(0, -5) * mm, "end": v(-20, -5) * mm});
            skLineSegment(sketch, "E26.left", {"start": v(0, -7) * mm, "end": v(0, -5) * mm});
            skLineSegment(sketch, "E26.right", {"start": v(-20, -7) * mm, "end": v(-20, -5) * mm});
            skSolve(sketch);
        }
        {
            var Q0;
            {var subQ0=sQuery(id+"F0.wireOp",EDGE,"E0.left");var subQ1=sQuery(id+"F0.wireOp",EDGE,"E0.bottom");Q0=makeQuery(id+"F8.boolean.opBoolean","MERGE",EDGE,{"derivedFrom":[makeQuery(id+"F5.opExtrude","CAP_EDGE",EDGE,{"disambiguationData":[OSD([subQ1,subQ0]),TDD([makeQuery(id+"F4.opExtrude","CAP_EDGE",EDGE,{"disambiguationData":[OSD([subQ1,subQ0])],"isStart":false})])],"isStart":false}),makeQuery(id+"F8.opExtrude","SWEPT_EDGE",EDGE,{"disambiguationData":[OSD([sQuery(id+"F7.wireOp",EDGE,"E9.top"),sQuery(id+"F7.wireOp",EDGE,"E16.trimOffspring")])]})]});}
            var Q1;
            {var subQ0=sQuery(id+"F0.wireOp",EDGE,"E0.right");var subQ1=sQuery(id+"F0.wireOp",EDGE,"E0.bottom");Q1=makeQuery(id+"F8.boolean.opBoolean","MERGE",EDGE,{"derivedFrom":[makeQuery(id+"F6.opExtrude","CAP_EDGE",EDGE,{"disambiguationData":[OSD([subQ1,subQ0]),TDD([makeQuery(id+"F4.opExtrude","CAP_EDGE",EDGE,{"disambiguationData":[OSD([subQ1,subQ0])],"isStart":false})])],"isStart":false}),makeQuery(id+"F8.opExtrude","SWEPT_EDGE",EDGE,{"disambiguationData":[OSD([sQuery(id+"F7.wireOp",EDGE,"E8.top"),sQuery(id+"F7.wireOp",EDGE,"E13.trimOffspring")])]})]});}
            var Q2;
            {var subQ0=sQuery(id+"F0.wireOp",EDGE,"E0.right");var subQ1=sQuery(id+"F0.wireOp",EDGE,"E0.bottom");var subQ2=sQuery(id+"F0.wireOp",EDGE,"E0.left");Q2=makeQuery(id+"F6.boolean.opBoolean","MERGE",EDGE,{"derivedFrom":[makeQuery(id+"F5.boolean.opBoolean","MERGE",EDGE,{"derivedFrom":[makeQuery(id+"F4.opExtrude","CAP_EDGE",EDGE,{"disambiguationData":[OSD([subQ1]),TDD([makeQuery(id+"F1.opExtrude","CAP_EDGE",EDGE,{"disambiguationData":[OSD([subQ1])],"isStart":false})])],"isStart":false}),makeQuery(id+"F5.opExtrude","SWEPT_EDGE",EDGE,{"disambiguationData":[OSD([subQ1,subQ2]),TDD([makeQuery(id+"F4.opExtrude","CAP_VERTEX",VERTEX,{"disambiguationData":[OSD([subQ1,subQ2]),TDD([makeQuery(id+"F1.opExtrude","CAP_VERTEX",VERTEX,{"disambiguationData":[OSD([subQ1,subQ2])],"isStart":false})])],"isStart":false})])]})]}),makeQuery(id+"F6.opExtrude","SWEPT_EDGE",EDGE,{"disambiguationData":[OSD([subQ1,subQ0]),TDD([makeQuery(id+"F4.opExtrude","CAP_VERTEX",VERTEX,{"disambiguationData":[OSD([subQ1,subQ0]),TDD([makeQuery(id+"F1.opExtrude","CAP_VERTEX",VERTEX,{"disambiguationData":[OSD([subQ1,subQ0])],"isStart":false})])],"isStart":false})])]})]});}
            var Q3;
            {var subQ0=sQuery(id+"F0.wireOp",EDGE,"E0.right");var subQ1=sQuery(id+"F0.wireOp",EDGE,"E0.bottom");Q3=makeQuery(id+"F14.boolean.opBoolean","MERGE",EDGE,{"derivedFrom":[makeQuery(id+"F6.opExtrude","CAP_EDGE",EDGE,{"disambiguationData":[OSD([subQ1,subQ0]),TDD([makeQuery(id+"F4.boolean.opBoolean","MERGE",EDGE,{"derivedFrom":[makeQuery(id+"F1.opExtrude","CAP_EDGE",EDGE,{"disambiguationData":[OSD([subQ0])],"isStart":false}),makeQuery(id+"F4.opExtrude","SWEPT_EDGE",EDGE,{"disambiguationData":[OSD([subQ1,subQ0]),TDD([makeQuery(id+"F1.opExtrude","CAP_VERTEX",VERTEX,{"disambiguationData":[OSD([subQ1,subQ0])],"isStart":false})])]})]})])],"isStart":false}),makeQuery(id+"F14.opExtrude","SWEPT_EDGE",EDGE,{"disambiguationData":[OSD([sQuery(id+"F13.wireOp",EDGE,"E24.bottom"),sQuery(id+"F13.wireOp",EDGE,"E24.left")])]})]});}
            var Q4;
            {var subQ0=sQuery(id+"F0.wireOp",EDGE,"E0.left");var subQ1=sQuery(id+"F0.wireOp",EDGE,"E0.bottom");Q4=makeQuery(id+"F12.boolean.opBoolean","MERGE",EDGE,{"derivedFrom":[makeQuery(id+"F5.opExtrude","CAP_EDGE",EDGE,{"disambiguationData":[OSD([subQ1,subQ0]),TDD([makeQuery(id+"F4.boolean.opBoolean","MERGE",EDGE,{"derivedFrom":[makeQuery(id+"F1.opExtrude","CAP_EDGE",EDGE,{"disambiguationData":[OSD([subQ0])],"isStart":false}),makeQuery(id+"F4.opExtrude","SWEPT_EDGE",EDGE,{"disambiguationData":[OSD([subQ1,subQ0]),TDD([makeQuery(id+"F1.opExtrude","CAP_VERTEX",VERTEX,{"disambiguationData":[OSD([subQ1,subQ0])],"isStart":false})])]})]})])],"isStart":false}),makeQuery(id+"F12.opExtrude","SWEPT_EDGE",EDGE,{"disambiguationData":[OSD([sQuery(id+"F11.wireOp",EDGE,"E23.bottom"),sQuery(id+"F11.wireOp",EDGE,"E23.left")])]})]});}
            fillet(context, id + "F16", {"entities" : qUnion([Q0, Q1, Q2, Q3, Q4]), "radius" : 2 * mm, "tangentPropagation" : true, "allowEdgeOverflow" : false});
        }
        {
            var Q0;
            Q0=makeQuery(id+"F15.imprint","IMPRINT",FACE,{"disambiguationData":[TD([[makeQuery(id+"F15.imprint","IMPRINT",EDGE,{"derivedFrom":sQuery(id+"F15.wireOp",EDGE,"E25.bottom")}),1.0]])]});
            var Q1;
            Q1=makeQuery(id+"F15.imprint","IMPRINT",FACE,{"disambiguationData":[TD([[makeQuery(id+"F15.imprint","IMPRINT",EDGE,{"derivedFrom":sQuery(id+"F15.wireOp",EDGE,"E26.bottom")}),1.0]])]});
            extrude(context, id + "F17", {"entities" : qUnion([Q0, Q1]), "operationType" : NewBodyOperationType.ADD, "depth" : 2 * mm, "offsetDistance" : 25 * mm});
        }
        {
            var Q0;
            Q0=makeQuery(id+"F17.opExtrude","CAP_EDGE",EDGE,{"disambiguationData":[OSD([sQuery(id+"F15.wireOp",EDGE,"E25.top")])],"isStart":false});
            var Q1;
            Q1=makeQuery(id+"F17.opExtrude","CAP_EDGE",EDGE,{"disambiguationData":[OSD([sQuery(id+"F15.wireOp",EDGE,"E25.bottom")])],"isStart":false});
            var Q2;
            Q2=makeQuery(id+"F17.opExtrude","CAP_EDGE",EDGE,{"disambiguationData":[OSD([sQuery(id+"F15.wireOp",EDGE,"E26.top")])],"isStart":false});
            var Q3;
            Q3=makeQuery(id+"F17.opExtrude","CAP_EDGE",EDGE,{"disambiguationData":[OSD([sQuery(id+"F15.wireOp",EDGE,"E26.bottom")])],"isStart":false});
            fillet(context, id + "F18", {"entities" : qUnion([Q0, Q1, Q2, Q3]), "radius" : 1 * mm, "tangentPropagation" : true, "allowEdgeOverflow" : false});
        }
        {
            var Q0;
            Q0=makeQuery(id+"F12.boolean.opBoolean","MERGE",FACE,{"derivedFrom":[makeQuery(id+"F8.boolean.opBoolean","MERGE",FACE,{"derivedFrom":[makeQuery(id+"F5.opExtrude","CAP_FACE",FACE,{"disambiguationData":[OSD([sQuery(id+"F0.wireOp",EDGE,"E0.bottom"),sQuery(id+"F0.wireOp",EDGE,"E0.left")])],"isStart":false}),makeQuery(id+"F8.opExtrude","SWEPT_FACE",FACE,{"disambiguationData":[OSD([sQuery(id+"F7.wireOp",EDGE,"E16.trimOffspring")])]})]}),makeQuery(id+"F12.opExtrude","SWEPT_FACE",FACE,{"disambiguationData":[OSD([sQuery(id+"F11.wireOp",EDGE,"E23.left")])]})]});
            var sketch = newSketch(context, id + "F19", { "sketchPlane" : qUnion([Q0])});
            skCircle(sketch, "E27", {"center": v(-112.75, -3.5) * mm, "radius": 1 * mm});
            skPoint(sketch, "E27.centerSnap0", {"position": v(-117.75, -3.5) * mm});
            skSolve(sketch);
        }
        {
            var Q0;
            Q0=makeQuery(id+"F19.imprint","IMPRINT",FACE,{"disambiguationData":[TD([[makeQuery(id+"F19.imprint","IMPRINT",EDGE,{"derivedFrom":sQuery(id+"F19.wireOp",EDGE,"E27")}),1.0]])]});
            extrude(context, id + "F20", {"entities" : qUnion([Q0]), "operationType" : NewBodyOperationType.REMOVE, "endBound" : BoundingType.THROUGH_ALL, "oppositeDirection" : true, "depth" : 25 * mm, "offsetDistance" : 25 * mm});
        }
        {
            var Q0;
            Q0=makeQuery(id+"F12.opExtrude","CAP_EDGE",EDGE,{"disambiguationData":[OSD([sQuery(id+"F11.wireOp",EDGE,"E23.top")])],"isStart":false});
            var Q1;
            Q1=makeQuery(id+"F14.opExtrude","CAP_EDGE",EDGE,{"disambiguationData":[OSD([sQuery(id+"F13.wireOp",EDGE,"E24.top")])],"isStart":false});
            var Q2;
            Q2=makeQuery(id+"F14.opExtrude","CAP_EDGE",EDGE,{"disambiguationData":[OSD([sQuery(id+"F13.wireOp",EDGE,"E24.bottom")])],"isStart":false});
            var Q3;
            Q3=makeQuery(id+"F12.opExtrude","CAP_EDGE",EDGE,{"disambiguationData":[OSD([sQuery(id+"F11.wireOp",EDGE,"E23.bottom")])],"isStart":false});
            fillet(context, id + "F21", {"entities" : qUnion([Q0, Q1, Q2, Q3]), "radius" : 5 * mm, "tangentPropagation" : true, "allowEdgeOverflow" : false});
        }
    });